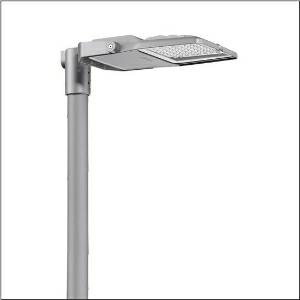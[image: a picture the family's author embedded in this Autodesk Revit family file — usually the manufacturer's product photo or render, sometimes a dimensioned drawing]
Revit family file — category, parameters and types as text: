
# Revit family: floodlight_fl_21_mini___pl43_5xa7776c2a3a_c8bd
name_source: partatom
category: Lighting Fixtures
units: mm (PartAtom-declared; Revit-internal decimal feet)

## family parameters
Cut with Voids When Loaded = No
Host = Face
Light Source = No
Part Type = Normal
Room Calculation Point = No
Round Connector Dimension = Use Diameter
Shared = No

## types (1)
- --- (1 x LED, 12500 lm, 89 W, 3000K)
    Apparent Load = 89 VA
    CIE Flux Codes = 27 78 99 100 100
    Color Rendering = 70
    Color Temperature = 3000K
    Default Elevation = 1800 mm
    Description = Floodlight FL 21 mini, floodlight, primary light control with lens, of PMMA, primary optical cover: protective disc, of toughened safety glass, transparent, light distribution: PL43, light emission: direct distribution, installation type: surface-mounted, LED, High Power LED, rated luminous flux: 12.500lm, luminous efficacy: 140lm/W, light colour: 730, colour temperature: 3000K, control gear: Smart Interface (Zhaga), control: flexible luminous flux parameterisation, time-dependent luminous flux control, constant luminous flux control, overheat protection, pre-setting: logarithmic dimming characteristic, with terminal, 6-pole, mains connection: 220..240V, AC, 50/60Hz, start of lifetime: 89W, end of service life: 94W, reduction: 43W, luminaire housing, of diecast aluminium, powder-coated, Siteco® metallic grey (DB 702S), corrosivity category C5 mid according to DIN EN ISO 12944, suitable for swimming pools, chlorine-resistant, sealing non-destructively replaceable, please order mast flange separately, mast bracket, of steel, galvanised, powder-coated, Siteco® metallic grey (DB 702S), Smart Interface below and above, protection rating (complete): IP66, insulation class (complete): insulation class II (safety insulation), certification: CE, ENEC, VDE, protection symbol: D, impact resistance: IK08, permissible operating ambient temperature: -40..+40°C, permissible operating ambient temperature for outdoor applications: -40..+50°C, standard: DIN EN 12944, LABS conformity tested according to VDMA 24364:2018-05, packaging unit: 1 piece

Light Distribution: PL43
    Height = 70 mm
    Lamp = 1 x LED
    Lamp Light Flux = 12500 lm
    Lamp Power = 89 W
    Lamp count = 1
    Length = 485 mm
    Luminous efficacy = 140 lm/W
    Manufacturer = Siteco
    ModVariant = No
    Model = 5XA7776C2A3A
    Number of Poles = 1
    OnlyDefault = Yes
    Power Factor = 1
    Product Name = Floodlight FL 21 mini | PL43
    Product group = floodlight | pylon annexe
    ProductGroupID = 6201
    Protection Class = Protection class II
    Protection Degree = IP 66
    RLX_Detail_Level = 1
    RLX_Emergency_Light_Flux = 0 lm
    RLX_Emergency_Type = 0
    RLX_Emergency_Type_DB = No
    RlxData = <blob elided: 100881 chars, md5=833669ee>
    Socket = socket
    Standby Power = 0 W
    System Light Flux = 12500 lm
    System Power = 89 W
    Type Comments = factory setting: luminous flux: 100 % | dim-lin: 254 | 456 mA
    Type Image = l_1007125.jpg
    URL = http://relux.com
    VarID = @adj_182537
    Voltage = 0 V
    Weight = 0.00 kg
    Width = 337 mm

## geometry (parser evidence)
native form markers: Blend x4, Sweep x13
no freeform markers — native parametric forms only
